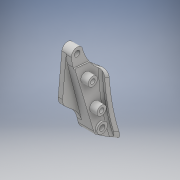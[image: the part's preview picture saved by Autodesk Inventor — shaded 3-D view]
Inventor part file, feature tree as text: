
AUTODESK INVENTOR PART (.ipt)
format: ipt  version: 2018 (Build 220112000, 112)  size: 358,912 bytes
history: native  units: mm
features: other x8, extrude x1, sketch x1, projected_geometry x1
ambient origin geometry x8: Origin, YZ Plane, XZ Plane, XY Plane, X Axis, Y Axis, Z Axis, Center Point
bodies: Body1 (feature_tree)
feature tree (11):
  other  "ソリッド1"
  other  "ダイレクト編集1"
  other  "ダイレクト編集2"
  extrude  "押し出し1"  Depth=8.8365mm
  other  "ダイレクト編集3"
  sketch  "スケッチ1"
  projected_geometry  "投影ループ1"
  other  "尺度1"
  other  "サイズ1"
  other  "サイズ2"
  other  "サイズ3"
